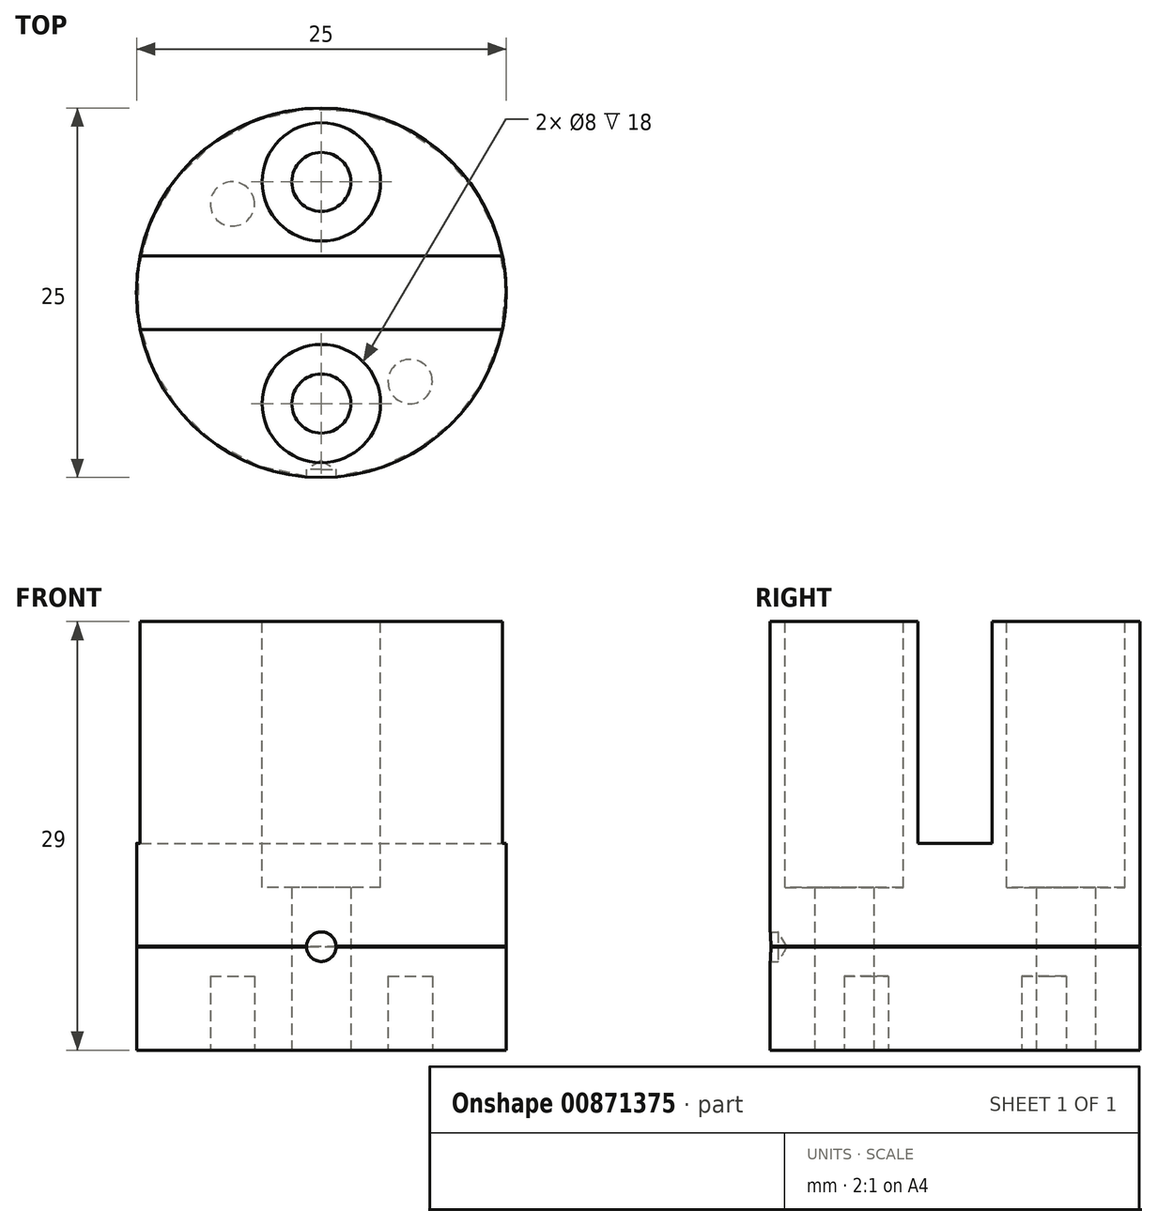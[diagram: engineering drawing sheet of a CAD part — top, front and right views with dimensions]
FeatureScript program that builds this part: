
annotation { "Feature Type Name" : "Feature", "Feature Type Description" : "" }
export const myFeature = defineFeature(function(context is Context, id is Id, definition is map)
    precondition{}
    {
        {
            var Q0;
            Q0=qCreatedBy(makeId("Top.planeOp"),FACE);
            var sketch = newSketch(context, id + "F0", { "sketchPlane" : qUnion([Q0])});
            skCircle(sketch, "E0", {"center": v(0, 0) * mm, "radius": 12.5 * mm});
            skSolve(sketch);
        }
        {
            var Q0;
            Q0 = qSketchRegion(id + "F0", true);
            extrude(context, id + "F1", {"entities" : qUnion([Q0]), "depth" : 29 * mm, "offsetDistance" : 25 * mm});
        }
        {
            var Q0;
            Q0=makeQuery(id+"F1.opExtrude","CAP_FACE",FACE,{"disambiguationData":[OSD([sQuery(id+"F0.wireOp",EDGE,"E0")])],"isStart":false});
            var sketch = newSketch(context, id + "F2", { "sketchPlane" : qUnion([Q0])});
            skLineSegment(sketch, "E1", {"start": v(-13.12, 2.5) * mm, "end": v(22.34, 2.5) * mm});
            skLineSegment(sketch, "E2.MirrorCS", {"start": v(-13.12, -2.5) * mm, "end": v(22.34, -2.5) * mm});
            skLineSegment(sketch, "E3", {"start": v(-13.12, 2.5) * mm, "end": v(-13.12, -2.5) * mm});
            skLineSegment(sketch, "E4", {"start": v(22.34, 2.5) * mm, "end": v(22.34, -2.5) * mm});
            skSolve(sketch);
        }
        {
            var Q0;
            Q0 = qSketchRegion(id + "F2", true);
            extrude(context, id + "F3", {"entities" : qUnion([Q0]), "operationType" : NewBodyOperationType.REMOVE, "oppositeDirection" : true, "depth" : 15 * mm, "offsetDistance" : 25 * mm});
        }
        {
            var Q0;
            {var subQ0=sQuery(id+"F0.wireOp",EDGE,"E0");Q0=makeQuery(id+"F3.boolean.opBoolean","SPLIT",FACE,{"disambiguationData":[TD([makeQuery(id+"F3.opExtrude","SWEPT_FACE",FACE,{"disambiguationData":[OSD([sQuery(id+"F2.wireOp",EDGE,"E1")])]})])],"derivedFrom":makeQuery(id+"F1.opExtrude","CAP_FACE",FACE,{"disambiguationData":[OSD([subQ0])],"isStart":false})});}
            var sketch = newSketch(context, id + "F4", { "sketchPlane" : qUnion([Q0])});
            skPoint(sketch, "E5", {"position": v(0, 7.5) * mm});
            skPoint(sketch, "E6", {"position": v(0, -7.5) * mm});
            skCircle(sketch, "E7", {"center": v(0, 7.5) * mm, "radius": 4 * mm});
            skCircle(sketch, "E8", {"center": v(0, -7.5) * mm, "radius": 4 * mm});
            skSolve(sketch);
        }
        {
            var Q0;
            Q0=sQuery(id+"F4.wireOp",VERTEX,"E5");
            var Q1;
            Q1=sQuery(id+"F4.wireOp",VERTEX,"E6");
            var Q2;
            Q2=makeQuery(id+"F1.opExtrude","SWEPT_BODY",BODY,{"disambiguationData":[OSD([sQuery(id+"F0.wireOp",EDGE,"E0")])]});
            hole(context, id + "F5", {"style" : HoleStyle.SIMPLE, "endStyle" : HoleEndStyle.THROUGH, "holeDiameter" : 4 * mm, "majorDiameter" : 5 * mm, "isTappedThrough" : true, "tappedDepth" : 12 * mm, "tapClearance" : 3, "locations" : qUnion([Q0, Q1]), "scope" : qUnion([Q2]), "startStyle" : HoleStartStyle.PART});
        }
        {
            var Q0;
            Q0=makeQuery(id+"F4.imprint","IMPRINT",FACE,{"disambiguationData":[TD([[makeQuery(id+"F4.imprint","IMPRINT",EDGE,{"derivedFrom":sQuery(id+"F4.wireOp",EDGE,"E7")}),1.0]])]});
            var Q1;
            Q1=makeQuery(id+"F4.imprint","IMPRINT",FACE,{"disambiguationData":[TD([[makeQuery(id+"F4.imprint","IMPRINT",EDGE,{"derivedFrom":sQuery(id+"F4.wireOp",EDGE,"E8")}),1.0]])]});
            var Q2;
            Q2=sQuery(id+"F4.wireOp",EDGE,"E7");
            var Q3;
            Q3=sQuery(id+"F4.wireOp",EDGE,"E8");
            extrude(context, id + "F6", {"entities" : qUnion([Q0, Q1]), "operationType" : NewBodyOperationType.REMOVE, "surfaceEntities" : qUnion([Q2, Q3]), "oppositeDirection" : true, "depth" : 18 * mm, "offsetDistance" : 25 * mm});
        }
        {
            var Q0;
            Q0=qCreatedBy(makeId("Front.planeOp"),FACE);
            cPlane(context, id + "F7", {"entities" : qUnion([Q0]), "cplaneType" : CPlaneType.OFFSET, "offset" : 12.5 * mm, "width" : 150 * mm, "height" : 150 * mm});
        }
        {
            var Q0;
            Q0=qCreatedBy(id+"F7.planeOp",FACE);
            var sketch = newSketch(context, id + "F8", { "sketchPlane" : qUnion([Q0])});
            skPoint(sketch, "E9", {"position": v(0, 7) * mm});
            skSolve(sketch);
        }
        {
            var Q0;
            Q0=sQuery(id+"F8.wireOp",VERTEX,"E9");
            var Q1;
            Q1=makeQuery(id+"F1.opExtrude","SWEPT_BODY",BODY,{"disambiguationData":[OSD([sQuery(id+"F0.wireOp",EDGE,"E0")])]});
            hole(context, id + "F9", {"style" : HoleStyle.SIMPLE, "endStyle" : HoleEndStyle.BLIND, "holeDiameter" : 2 * mm, "majorDiameter" : 5 * mm, "holeDepth" : .5 * mm, "isTappedThrough" : true, "tappedDepth" : 12 * mm, "tapClearance" : 3, "locations" : qUnion([Q0]), "scope" : qUnion([Q1]), "startStyle" : HoleStartStyle.PART});
        }
        {
            var Q0;
            Q0=qCreatedBy(makeId("Front.planeOp"),FACE);
            var sketch = newSketch(context, id + "F10", { "sketchPlane" : qUnion([Q0])});
            skPoint(sketch, "E10", {"position": v(12.5, 7) * mm});
            skCircle(sketch, "E11", {"center": v(12.5, 7) * mm, "radius": 0.02 * mm});
            skLineSegment(sketch, "E12", {"start": v(0, 41.22) * mm, "end": v(0, -32.92) * mm, "construction": true});
            skSolve(sketch);
        }
        {
            var Q0;
            Q0 = qSketchRegion(id + "F10", true);
            var Q1;
            Q1=sQuery(id+"F10.wireOp",EDGE,"E12");
            revolve(context, id + "F11", {"operationType" : NewBodyOperationType.REMOVE, "surfaceOperationType" : NewSurfaceOperationType.NEW, "entities" : qUnion([Q0]), "axis" : qUnion([Q1]), "revolveType" : RevolveType.FULL});
        }
        {
            var Q0;
            Q0=makeQuery(id+"F1.opExtrude","CAP_FACE",FACE,{"disambiguationData":[OSD([sQuery(id+"F0.wireOp",EDGE,"E0")])],"isStart":true});
            var sketch = newSketch(context, id + "F12", { "sketchPlane" : qUnion([Q0])});
            skLineSegment(sketch, "E13", {"start": v(-13.59, -13.59) * mm, "end": v(12.48, 12.48) * mm, "construction": true});
            skPoint(sketch, "E14", {"position": v(6.01, 6.01) * mm});
            skPoint(sketch, "E15", {"position": v(-6.01, -6.01) * mm});
            skCircle(sketch, "E16", {"center": v(6.01, 6.01) * mm, "radius": 1.5 * mm});
            skCircle(sketch, "E17", {"center": v(-6.01, -6.01) * mm, "radius": 1.5 * mm});
            skSolve(sketch);
        }
        {
            var Q0;
            Q0=makeQuery(id+"F12.imprint","IMPRINT",FACE,{"disambiguationData":[TD([[makeQuery(id+"F12.imprint","IMPRINT",EDGE,{"derivedFrom":sQuery(id+"F12.wireOp",EDGE,"E16")}),1.0]])]});
            var Q1;
            Q1=makeQuery(id+"F12.imprint","IMPRINT",FACE,{"disambiguationData":[TD([[makeQuery(id+"F12.imprint","IMPRINT",EDGE,{"derivedFrom":sQuery(id+"F12.wireOp",EDGE,"E17")}),1.0]])]});
            var Q2;
            Q2=sQuery(id+"F12.wireOp",EDGE,"E17");
            var Q3;
            Q3=sQuery(id+"F12.wireOp",EDGE,"E16");
            extrude(context, id + "F13", {"entities" : qUnion([Q0, Q1]), "operationType" : NewBodyOperationType.REMOVE, "surfaceEntities" : qUnion([Q2, Q3]), "oppositeDirection" : true, "depth" : 5 * mm, "offsetDistance" : 25 * mm});
        }
    });
